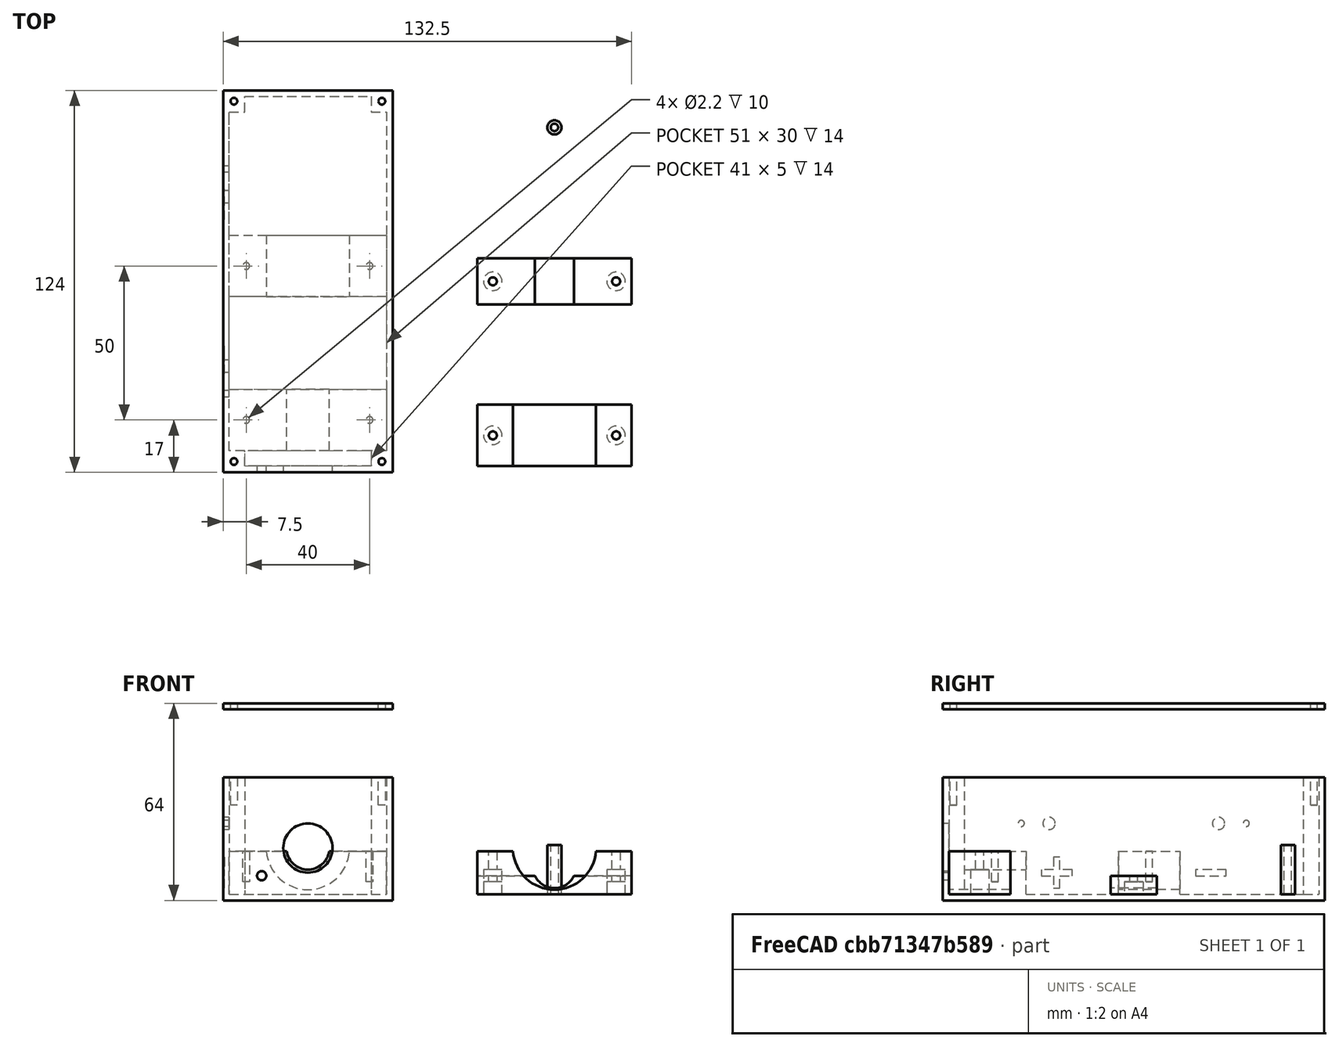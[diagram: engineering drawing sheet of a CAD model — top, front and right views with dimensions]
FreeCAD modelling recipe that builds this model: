
FCSTD DOCUMENT  (FreeCAD 0.20R29410 (Git))
Label: smoker_parts
License: All rights reserved
LicenseURL: http://en.wikipedia.org/wiki/All_rights_reserved
objects: Sketcher::SketchObject×23, PartDesign::Pocket×17, PartDesign::Pad×6, PartDesign::Body×5, Mesh::Feature×5
note: 74 computed .brp shape members not serialized (recipe doc carries the construction recipe); baked Part::Feature solids carry a one-line shape summary decoded from their .brp

FEATURE [Sketcher::SketchObject] Sketch
  FullyConstrained = true
  MapMode = 5
  Support = -> [XY_Plane]
  sketch-geometry (4):
    g0: LineSegment StartX=-25 StartY=7.5 StartZ=0 EndX=25 EndY=7.5 EndZ=0
    g1: LineSegment StartX=25 StartY=7.5 StartZ=0 EndX=25 EndY=-7.5 EndZ=0
    g2: LineSegment StartX=25 StartY=-7.5 StartZ=0 EndX=-25 EndY=-7.5 EndZ=0
    g3: LineSegment StartX=-25 StartY=-7.5 StartZ=0 EndX=-25 EndY=7.5 EndZ=0
  constraints (12):
    c: Coincident(g0,g1)
    c: Coincident(g1,g2)
    c: Coincident(g2,g3)
    c: Coincident(g3,g0)
    c: Horizontal(g0)
    c: Horizontal(g2)
    c: Vertical(g1)
    c: Vertical(g3)
    c: DistanceX(g0,g0) = 50
    c: DistanceY(g1,g1) = 15
    c: DistanceX(g-1,g0) = 25
    c: DistanceY(g1,g-1) = 7.5
FEATURE [PartDesign::Pad] Pad
  Direction = (1,1,1)
  Length = 6
  Length2 = 100
  Profile = -> Sketch
  Type = 0
FEATURE [Sketcher::SketchObject] Sketch001
  FullyConstrained = true
  MapMode = 5
  Placement = pos=(0,-7.5,0) rot=(1,0,0;1.5708rad)
  Support = -> [Pad]
  sketch-geometry (1):
    g0: Circle CenterX=0 CenterY=9 CenterZ=0 NormalX=0 NormalY=0 NormalZ=1 AngleXU=0 Radius=7
  constraints (3):
    c: PointOnObject(g0,g-2)
    c: Radius(g0) = 7
    c: DistanceY(g-1,g0) = 9
FEATURE [PartDesign::Pocket] Pocket
  BaseFeature = -> Pad
  Direction = (1,1,1)
  Length = 5
  Length2 = 100
  Profile = -> Sketch001
  Type = 1
FEATURE [Sketcher::SketchObject] Sketch002
  FullyConstrained = true
  MapMode = 5
  Placement = pos=(0,0,6) rot=(0,0,1;0rad)
  Support = -> [Pad]
  sketch-geometry (2):
    g0: Circle CenterX=-20 CenterY=0 CenterZ=0 NormalX=0 NormalY=0 NormalZ=1 AngleXU=0 Radius=1.3
    g1: Circle CenterX=20 CenterY=0 CenterZ=0 NormalX=0 NormalY=0 NormalZ=1 AngleXU=0 Radius=1.3
  constraints (6):
    c: PointOnObject(g0,g-1)
    c: PointOnObject(g1,g-1)
    c: Equal(g1,g0)
    c: Radius(g0) = 1.3
    c: DistanceX(g0,g1) = 40
    c: DistanceX(g-1,g1) = 20
FEATURE [PartDesign::Pocket] Pocket001
  BaseFeature = -> Pocket
  Direction = (1,1,1)
  Length = 5
  Length2 = 100
  Profile = -> Sketch002
  Type = 1
FEATURE [Sketcher::SketchObject] Sketch003
  FullyConstrained = true
  MapMode = 5
  Support = -> [XY_Plane001]
  sketch-geometry (4):
    g0: LineSegment StartX=-25 StartY=10 StartZ=0 EndX=25 EndY=10 EndZ=0
    g1: LineSegment StartX=25 StartY=10 StartZ=0 EndX=25 EndY=-10 EndZ=0
    g2: LineSegment StartX=25 StartY=-10 StartZ=0 EndX=-25 EndY=-10 EndZ=0
    g3: LineSegment StartX=-25 StartY=-10 StartZ=0 EndX=-25 EndY=10 EndZ=0
  constraints (12):
    c: Coincident(g0,g1)
    c: Coincident(g1,g2)
    c: Coincident(g2,g3)
    c: Coincident(g3,g0)
    c: Horizontal(g0)
    c: Horizontal(g2)
    c: Vertical(g1)
    c: Vertical(g3)
    c: DistanceX(g0,g0) = 50
    c: DistanceY(g1,g1) = 20
    c: DistanceY(g-1,g0) = 10
    c: DistanceX(g-1,g0) = 25
FEATURE [PartDesign::Pad] Pad001
  Direction = (1,1,1)
  Length = 14
  Length2 = 100
  Profile = -> Sketch003
  Type = 0
FEATURE [Sketcher::SketchObject] Sketch004
  FullyConstrained = true
  MapMode = 5
  Placement = pos=(0,-10,0) rot=(1,0,0;1.5708rad)
  Support = -> [Pad001]
  sketch-geometry (1):
    g0: Circle CenterX=0 CenterY=15 CenterZ=0 NormalX=0 NormalY=0 NormalZ=1 AngleXU=0 Radius=13.5
  constraints (3):
    c: PointOnObject(g0,g-2)
    c: Radius(g0) = 13.5
    c: DistanceY(g-1,g0) = 15
FEATURE [PartDesign::Pocket] Pocket002
  BaseFeature = -> Pad001
  Direction = (1,1,1)
  Length = 5
  Length2 = 100
  Profile = -> Sketch004
  Type = 1
FEATURE [Sketcher::SketchObject] Sketch005
  FullyConstrained = true
  MapMode = 5
  Placement = pos=(0,0,14) rot=(0,0,1;0rad)
  Support = -> [Pocket002]
  sketch-geometry (2):
    g0: Circle CenterX=-20 CenterY=0 CenterZ=0 NormalX=0 NormalY=0 NormalZ=1 AngleXU=0 Radius=1.3
    g1: Circle CenterX=20 CenterY=0 CenterZ=0 NormalX=0 NormalY=0 NormalZ=1 AngleXU=0 Radius=1.3
  constraints (6):
    c: PointOnObject(g0,g-1)
    c: PointOnObject(g1,g-1)
    c: Equal(g1,g0)
    c: Radius(g0) = 1.3
    c: DistanceX(g0,g1) = 40
    c: DistanceX(g-1,g1) = 20
FEATURE [PartDesign::Pocket] Pocket003
  BaseFeature = -> Pocket002
  Direction = (1,1,1)
  Length = 5
  Length2 = 100
  Profile = -> Sketch005
  Type = 1
FEATURE [Sketcher::SketchObject] Sketch006
  FullyConstrained = true
  MapMode = 5
  Support = -> [XY_Plane002]
  sketch-geometry (4):
    g0: LineSegment StartX=-27.5 StartY=62 StartZ=0 EndX=27.5 EndY=62 EndZ=0
    g1: LineSegment StartX=27.5 StartY=62 StartZ=0 EndX=27.5 EndY=-62 EndZ=0
    g2: LineSegment StartX=27.5 StartY=-62 StartZ=0 EndX=-27.5 EndY=-62 EndZ=0
    g3: LineSegment StartX=-27.5 StartY=-62 StartZ=0 EndX=-27.5 EndY=62 EndZ=0
  constraints (12):
    c: Coincident(g0,g1)
    c: Coincident(g1,g2)
    c: Coincident(g2,g3)
    c: Coincident(g3,g0)
    c: Horizontal(g0)
    c: Horizontal(g2)
    c: Vertical(g1)
    c: Vertical(g3)
    c: DistanceX(g0,g0) = 55
    c: DistanceX(g-1,g0) = 27.5
    c: DistanceY(g1,g1) = 124
    c: DistanceY(g1,g-1) = 62
FEATURE [PartDesign::Pad] Pad002
  Direction = (1,1,1)
  Length = 40
  Length2 = 100
  Profile = -> Sketch006
  Type = 0
FEATURE [Sketcher::SketchObject] Sketch007
  FullyConstrained = true
  MapMode = 5
  Placement = pos=(0,0,40) rot=(0,0,1;0rad)
  Support = -> [Pad002]
  sketch-geometry (12):
    g0: LineSegment StartX=-25.5 StartY=55 StartZ=0 EndX=-20.5 EndY=55 EndZ=0
    g1: LineSegment StartX=-20.5 StartY=55 StartZ=0 EndX=-20.5 EndY=60 EndZ=0
    g2: LineSegment StartX=-20.5 StartY=60 StartZ=0 EndX=20.5 EndY=60 EndZ=0
    g3: LineSegment StartX=20.5 StartY=60 StartZ=0 EndX=20.5 EndY=55 EndZ=0
    g4: LineSegment StartX=20.5 StartY=55 StartZ=0 EndX=25.5 EndY=55 EndZ=0
    g5: LineSegment StartX=25.5 StartY=55 StartZ=0 EndX=25.5 EndY=-55 EndZ=0
    g6: LineSegment StartX=25.5 StartY=-55 StartZ=0 EndX=20.5 EndY=-55 EndZ=0
    g7: LineSegment StartX=20.5 StartY=-55 StartZ=0 EndX=20.5 EndY=-60 EndZ=0
    g8: LineSegment StartX=20.5 StartY=-60 StartZ=0 EndX=-20.5 EndY=-60 EndZ=0
    g9: LineSegment StartX=-20.5 StartY=-60 StartZ=0 EndX=-20.5 EndY=-55 EndZ=0
    g10: LineSegment StartX=-20.5 StartY=-55 StartZ=0 EndX=-25.5 EndY=-55 EndZ=0
    g11: LineSegment StartX=-25.5 StartY=-55 StartZ=0 EndX=-25.5 EndY=55 EndZ=0
  constraints (36):
    c: Coincident(g0,g1)
    c: Vertical(g1)
    c: Coincident(g1,g2)
    c: Horizontal(g2)
    c: Coincident(g2,g3)
    c: Coincident(g3,g4)
    c: Horizontal(g4)
    c: Coincident(g4,g5)
    c: Vertical(g5)
    c: Coincident(g5,g6)
    c: Coincident(g6,g7)
    c: Coincident(g7,g8)
    c: Horizontal(g8)
    c: Coincident(g8,g9)
    c: Coincident(g9,g10)
    c: Horizontal(g10)
    c: Coincident(g10,g11)
    c: Coincident(g11,g0)
    c: Vertical(g11)
    c: Horizontal(g0)
    c: Vertical(g3)
    c: Horizontal(g6)
    c: Vertical(g7)
    c: Vertical(g9)
    c: Equal(g6,g10)
    c: Equal(g4,g0)
    c: Equal(g1,g3)
    c: DistanceX(g6,g6) = 5
    c: DistanceY(g7,g7) = 5
    c: DistanceX(g2,g2) = 41
    c: DistanceX(g-1,g2) = 20.5
    c: DistanceX(g4,g4) = 5
    c: DistanceY(g3,g3) = 5
    c: DistanceY(g9,g9) = 5
    c: DistanceY(g5,g5) = 110
    c: DistanceY(g-1,g4) = 55
FEATURE [PartDesign::Pocket] Pocket004
  BaseFeature = -> Pad002
  Direction = (1,1,1)
  Length = 38
  Length2 = 100
  Profile = -> Sketch007
  Type = 0
FEATURE [Sketcher::SketchObject] Sketch008
  FullyConstrained = true
  MapMode = 5
  Placement = pos=(0,-62,0) rot=(1,0,0;1.5708rad)
  Support = -> [Pocket004]
  sketch-geometry (1):
    g0: Circle CenterX=0 CenterY=17 CenterZ=0 NormalX=0 NormalY=0 NormalZ=1 AngleXU=0 Radius=8
  constraints (3):
    c: PointOnObject(g0,g-2)
    c: Radius(g0) = 8
    c: DistanceY(g-1,g0) = 17
FEATURE [Sketcher::SketchObject] Sketch014
  FullyConstrained = true
  MapMode = 5
  Support = -> [XY_Plane004]
  sketch-geometry (4):
    g0: LineSegment StartX=-27.5 StartY=62 StartZ=0 EndX=27.5 EndY=62 EndZ=0
    g1: LineSegment StartX=27.5 StartY=62 StartZ=0 EndX=27.5 EndY=-62 EndZ=0
    g2: LineSegment StartX=27.5 StartY=-62 StartZ=0 EndX=-27.5 EndY=-62 EndZ=0
    g3: LineSegment StartX=-27.5 StartY=-62 StartZ=0 EndX=-27.5 EndY=62 EndZ=0
  constraints (12):
    c: Coincident(g0,g1)
    c: Coincident(g1,g2)
    c: Coincident(g2,g3)
    c: Coincident(g3,g0)
    c: Horizontal(g0)
    c: Horizontal(g2)
    c: Vertical(g1)
    c: Vertical(g3)
    c: DistanceX(g0,g0) = 55
    c: DistanceY(g1,g1) = 124
    c: DistanceX(g-1,g0) = 27.5
    c: DistanceY(g-1,g0) = 62
FEATURE [PartDesign::Pad] Pad004
  Direction = (1,1,1)
  Length = 2
  Length2 = 100
  Profile = -> Sketch014
  Type = 0
FEATURE [Sketcher::SketchObject] Sketch015
  FullyConstrained = true
  MapMode = 5
  Placement = pos=(0,0,2) rot=(0,0,1;0rad)
  Support = -> [Pad004]
  sketch-geometry (4):
    g0: Circle CenterX=-24 CenterY=58.5 CenterZ=0 NormalX=0 NormalY=0 NormalZ=1 AngleXU=0 Radius=1.1
    g1: Circle CenterX=24 CenterY=58.5 CenterZ=0 NormalX=0 NormalY=0 NormalZ=1 AngleXU=0 Radius=1.1
    g2: Circle CenterX=-24 CenterY=-58.5 CenterZ=0 NormalX=0 NormalY=0 NormalZ=1 AngleXU=0 Radius=1.1
    g3: Circle CenterX=24 CenterY=-58.5 CenterZ=0 NormalX=0 NormalY=0 NormalZ=1 AngleXU=0 Radius=1.1
  constraints (12):
    c: Radius(g0) = 1.1
    c: Equal(g0,g1)
    c: Equal(g2,g0)
    c: Equal(g0,g3)
    c: DistanceX(g0,g1) = 48
    c: DistanceX(g2,g0) = 0
    c: DistanceX(g0,g-1) = 24
    c: DistanceY(g1,g0) = 0
    c: DistanceY(g-1,g0) = 58.5
    c: DistanceY(g2,g0) = 117
    c: DistanceY(g2,g3) = 0
    c: DistanceX(g2,g3) = 48
FEATURE [PartDesign::Pocket] Pocket010
  BaseFeature = -> Pad004
  Direction = (1,1,1)
  Length = 2
  Length2 = 100
  Profile = -> Sketch015
  Type = 0
FEATURE [PartDesign::Body] Body004  label="Enclosure_lid"
  Group = -> [Sketch014,Pad004,Sketch015,Pocket010]
  Origin = -> Origin004
  Placement = pos=(0,0,60) rot=(0,0,1;0rad)
  Tip = -> Pocket010
FEATURE [Sketcher::SketchObject] Sketch017
  FullyConstrained = true
  MapMode = 5
  Placement = pos=(0,0,0) rot=(1,0,0;3.14159rad)
  Support = -> [Pocket003]
  sketch-geometry (2):
    g0: Circle CenterX=-20 CenterY=0 CenterZ=0 NormalX=0 NormalY=0 NormalZ=1 AngleXU=0 Radius=3
    g1: Circle CenterX=20 CenterY=0 CenterZ=0 NormalX=0 NormalY=0 NormalZ=1 AngleXU=0 Radius=3
  constraints (6):
    c: PointOnObject(g0,g-1)
    c: PointOnObject(g1,g-1)
    c: Radius(g0) = 3
    c: Equal(g0,g1)
    c: DistanceX(g0,g1) = 40
    c: DistanceX(g-1,g1) = 20
FEATURE [PartDesign::Pocket] Pocket012
  BaseFeature = -> Pocket003
  Direction = (1,1,1)
  Length = 8
  Length2 = 100
  Profile = -> Sketch017
  Type = 0
FEATURE [PartDesign::Body] Body001  label="pump"
  Group = -> [Sketch003,Pad001,Sketch004,Pocket002,Sketch005,Pocket003,Sketch017,Pocket012]
  Origin = -> Origin001
  Placement = pos=(80,-50,0) rot=(0,0,1;0rad)
  Tip = -> Pocket012
FEATURE [Sketcher::SketchObject] Sketch018
  FullyConstrained = true
  MapMode = 5
  Placement = pos=(0,0,0) rot=(1,0,0;3.14159rad)
  Support = -> [Pocket001]
  sketch-geometry (2):
    g0: Circle CenterX=-20 CenterY=0 CenterZ=0 NormalX=0 NormalY=0 NormalZ=1 AngleXU=0 Radius=3
    g1: Circle CenterX=20 CenterY=0 CenterZ=0 NormalX=0 NormalY=0 NormalZ=1 AngleXU=0 Radius=3
  constraints (6):
    c: PointOnObject(g0,g-1)
    c: PointOnObject(g1,g-1)
    c: Radius(g0) = 3
    c: Equal(g0,g1)
    c: DistanceX(g0,g1) = 40
    c: DistanceX(g-1,g1) = 20
FEATURE [PartDesign::Pocket] Pocket013
  BaseFeature = -> Pocket001
  Direction = (1,1,1)
  Length = 4
  Length2 = 100
  Profile = -> Sketch018
  Type = 0
FEATURE [PartDesign::Body] Body  label="chamber"
  Group = -> [Sketch,Pad,Sketch001,Pocket,Sketch002,Pocket001,Sketch018,Pocket013]
  Origin = -> Origin
  Placement = pos=(80,0,0) rot=(0,0,1;0rad)
  Tip = -> Pocket013
FEATURE [PartDesign::Pocket] Pocket005
  BaseFeature = -> Pocket004
  Direction = (1,1,1)
  Length = 2
  Length2 = 100
  Profile = -> Sketch008
  Type = 0
FEATURE [Sketcher::SketchObject] Sketch009
  FullyConstrained = true
  MapMode = 5
  Placement = pos=(0,0,40) rot=(0,0,1;0rad)
  Support = -> [Pocket005]
  sketch-geometry (4):
    g0: Circle CenterX=-24 CenterY=58.5 CenterZ=0 NormalX=0 NormalY=0 NormalZ=1 AngleXU=0 Radius=1.1
    g1: Circle CenterX=24 CenterY=58.5 CenterZ=0 NormalX=0 NormalY=0 NormalZ=1 AngleXU=0 Radius=1.1
    g2: Circle CenterX=24 CenterY=-58.5 CenterZ=0 NormalX=0 NormalY=0 NormalZ=1 AngleXU=0 Radius=1.1
    g3: Circle CenterX=-24 CenterY=-58.5 CenterZ=0 NormalX=0 NormalY=0 NormalZ=1 AngleXU=0 Radius=1.1
  constraints (12):
    c: Equal(g1,g0)
    c: Equal(g3,g0)
    c: Equal(g2,g0)
    c: Radius(g0) = 1.1
    c: DistanceY(g0,g1) = 0
    c: DistanceX(g0,g1) = 48
    c: DistanceX(g3,g2) = 48
    c: DistanceY(g3,g2) = 0
    c: DistanceX(g0,g3) = 0
    c: DistanceY(g3,g0) = 117
    c: DistanceX(g3,g-1) = 24
    c: DistanceY(g3,g-1) = 58.5
FEATURE [PartDesign::Pocket] Pocket006
  BaseFeature = -> Pocket005
  Direction = (1,1,1)
  Length = 9
  Length2 = 100
  Profile = -> Sketch009
  Type = 0
FEATURE [Sketcher::SketchObject] Sketch012
  FullyConstrained = true
  MapMode = 5
  Placement = pos=(-27.5,0,0) rot=(0.57735,-0.57735,-0.57735;2.0944rad)
  Support = -> [Pocket006]
  sketch-geometry (4):
    g0: Circle CenterX=-27.5 CenterY=25 CenterZ=0 NormalX=0 NormalY=0 NormalZ=1 AngleXU=0 Radius=2
    g1: Circle CenterX=27.5 CenterY=25 CenterZ=0 NormalX=0 NormalY=0 NormalZ=1 AngleXU=0 Radius=2
    g2: Circle CenterX=-36.5 CenterY=25 CenterZ=0 NormalX=0 NormalY=0 NormalZ=1 AngleXU=0 Radius=1
    g3: Circle CenterX=36.5 CenterY=25 CenterZ=0 NormalX=0 NormalY=0 NormalZ=1 AngleXU=0 Radius=1
  constraints (12):
    c: DistanceX(g0,g1) = 55
    c: DistanceY(g1,g0) = 0
    c: Equal(g1,g0)
    c: Radius(g0) = 2
    c: DistanceX(g2,g3) = 73
    c: DistanceY(g2,g3) = 0
    c: DistanceY(g1,g3) = 0
    c: Equal(g3,g2)
    c: Radius(g3) = 1
    c: DistanceX(g-1,g1) = 27.5
    c: DistanceX(g-1,g3) = 36.5
    c: DistanceY(g-1,g1) = 25
FEATURE [PartDesign::Pocket] Pocket008
  BaseFeature = -> Pocket006
  Direction = (1,1,1)
  Length = 2
  Length2 = 100
  Profile = -> Sketch012
  Type = 0
FEATURE [Sketcher::SketchObject] Sketch013
  FullyConstrained = true
  MapMode = 5
  Placement = pos=(0,-62,0) rot=(1,0,0;1.5708rad)
  Support = -> [Pocket008]
  sketch-geometry (1):
    g0: Circle CenterX=-15 CenterY=8 CenterZ=0 NormalX=0 NormalY=0 NormalZ=1 AngleXU=0 Radius=1.5
  constraints (3):
    c: Radius(g0) = 1.5
    c: DistanceX(g0,g-1) = 15
    c: DistanceY(g-1,g0) = 8
FEATURE [PartDesign::Pocket] Pocket009
  BaseFeature = -> Pocket008
  Direction = (1,1,1)
  Length = 2
  Length2 = 100
  Profile = -> Sketch013
  Type = 0
FEATURE [Sketcher::SketchObject] Sketch016
  FullyConstrained = true
  MapMode = 5
  Placement = pos=(-27.5,0,0) rot=(0.57735,-0.57735,-0.57735;2.0944rad)
  Support = -> [Pocket009]
  sketch-geometry (16):
    g0: LineSegment StartX=-30 StartY=10 StartZ=0 EndX=-20 EndY=10 EndZ=0
    g1: LineSegment StartX=-20 StartY=10 StartZ=0 EndX=-20 EndY=8 EndZ=0
    g2: LineSegment StartX=-20 StartY=8 StartZ=0 EndX=-30 EndY=8 EndZ=0
    g3: LineSegment StartX=-30 StartY=8 StartZ=0 EndX=-30 EndY=10 EndZ=0
    g4: LineSegment StartX=20 StartY=10 StartZ=0 EndX=24 EndY=10 EndZ=0
    g5: LineSegment StartX=30 StartY=10 StartZ=0 EndX=30 EndY=8 EndZ=0
    g6: LineSegment StartX=30 StartY=8 StartZ=0 EndX=26 EndY=8 EndZ=0
    g7: LineSegment StartX=20 StartY=8 StartZ=0 EndX=20 EndY=10 EndZ=0
    g8: LineSegment StartX=24 StartY=14 StartZ=0 EndX=26 EndY=14 EndZ=0
    g9: LineSegment StartX=26 StartY=14 StartZ=0 EndX=26 EndY=10 EndZ=0
    g10: LineSegment StartX=26 StartY=4 StartZ=0 EndX=24 EndY=4 EndZ=0
    g11: LineSegment StartX=24 StartY=4 StartZ=0 EndX=24 EndY=8 EndZ=0
    g12: LineSegment StartX=26 StartY=10 StartZ=0 EndX=30 EndY=10 EndZ=0
    g13: LineSegment StartX=24 StartY=10 StartZ=0 EndX=24 EndY=14 EndZ=0
    g14: LineSegment StartX=26 StartY=8 StartZ=0 EndX=26 EndY=4 EndZ=0
    g15: LineSegment StartX=24 StartY=8 StartZ=0 EndX=20 EndY=8 EndZ=0
  constraints (44):
    c: Coincident(g0,g1)
    c: Coincident(g1,g2)
    c: Coincident(g2,g3)
    c: Coincident(g3,g0)
    c: Horizontal(g0)
    c: Horizontal(g2)
    c: Vertical(g1)
    c: Vertical(g3)
    c: DistanceX(g0,g0) = 10
    c: DistanceY(g1,g1) = 2
    c: Coincident(g12,g5)
    c: Coincident(g5,g6)
    c: Coincident(g15,g7)
    c: Coincident(g7,g4)
    c: Horizontal(g4)
    c: Horizontal(g6)
    c: Vertical(g5)
    c: Vertical(g7)
    c: Coincident(g8,g9)
    c: Coincident(g14,g10)
    c: Coincident(g10,g11)
    c: Coincident(g13,g8)
    c: Horizontal(g8)
    c: Horizontal(g10)
    c: Vertical(g9)
    c: Vertical(g11)
    c: DistanceX(g4,g12) = 10
    c: DistanceX(g10,g10) = 2
    c: DistanceY(g14,g9) = 10
    c: DistanceY(g5,g5) = 2
    c: DistanceX(g4,g8) = 4
    c: DistanceY(g4,g8) = 4
    c: DistanceY(g0,g4) = 0
    c: DistanceX(g1,g15) = 40
    c: DistanceX(g1,g-1) = 20
    c: DistanceY(g-1,g1) = 8
    c: Tangent(g4,g12)
    c: Coincident(g13,g4)
    c: Tangent(g11,g13)
    c: Coincident(g9,g12)
    c: Tangent(g9,g14)
    c: Coincident(g6,g14)
    c: Coincident(g15,g11)
    c: Tangent(g6,g15)
FEATURE [PartDesign::Pocket] Pocket011
  BaseFeature = -> Pocket009
  Direction = (1,1,1)
  Length = 0.4
  Length2 = 100
  Profile = -> Sketch016
  Type = 0
FEATURE [Sketcher::SketchObject] Sketch019
  FullyConstrained = true
  MapMode = 5
  Placement = pos=(0,0,2) rot=(0,0,1;0rad)
  Support = -> [Pocket011]
  sketch-geometry (8):
    g0: LineSegment StartX=-25.5 StartY=15 StartZ=0 EndX=25.5 EndY=15 EndZ=0
    g1: LineSegment StartX=25.5 StartY=15 StartZ=0 EndX=25.5 EndY=-5 EndZ=0
    g2: LineSegment StartX=25.5 StartY=-5 StartZ=0 EndX=-25.5 EndY=-5 EndZ=0
    g3: LineSegment StartX=-25.5 StartY=-5 StartZ=0 EndX=-25.5 EndY=15 EndZ=0
    g4: LineSegment StartX=-25.5 StartY=-35 StartZ=0 EndX=25.5 EndY=-35 EndZ=0
    g5: LineSegment StartX=25.5 StartY=-35 StartZ=0 EndX=25.5 EndY=-55 EndZ=0
    g6: LineSegment StartX=25.5 StartY=-55 StartZ=0 EndX=-25.5 EndY=-55 EndZ=0
    g7: LineSegment StartX=-25.5 StartY=-55 StartZ=0 EndX=-25.5 EndY=-35 EndZ=0
  constraints (24):
    c: Coincident(g0,g1)
    c: Coincident(g1,g2)
    c: Coincident(g2,g3)
    c: Coincident(g3,g0)
    c: Horizontal(g0)
    c: Horizontal(g2)
    c: Vertical(g1)
    c: Vertical(g3)
    c: Coincident(g4,g5)
    c: Coincident(g5,g6)
    c: Coincident(g6,g7)
    c: Coincident(g7,g4)
    c: Horizontal(g4)
    c: Horizontal(g6)
    c: Vertical(g5)
    c: Vertical(g7)
    c: DistanceX(g2,g2) = 51
    c: DistanceX(g4,g4) = 51
    c: DistanceX(g-1,g4) = 25.5
    c: DistanceX(g-1,g1) = 25.5
    c: DistanceY(g1,g1) = 20
    c: DistanceY(g5,g5) = 20
    c: DistanceY(g4,g1) = 30
    c: DistanceY(g-1,g0) = 15
FEATURE [PartDesign::Pad] Pad005
  BaseFeature = -> Pocket011
  Direction = (1,1,1)
  Length = 14
  Length2 = 100
  Profile = -> Sketch019
  Type = 0
FEATURE [Sketcher::SketchObject] Sketch020
  FullyConstrained = true
  MapMode = 5
  Placement = pos=(0,-5,0) rot=(1,0,0;1.5708rad)
  Support = -> [Pad005]
  sketch-geometry (1):
    g0: Circle CenterX=0 CenterY=17 CenterZ=0 NormalX=0 NormalY=0 NormalZ=1 AngleXU=0 Radius=13.5
  constraints (3):
    c: PointOnObject(g0,g-2)
    c: Radius(g0) = 13.5
    c: DistanceY(g-1,g0) = 17
FEATURE [Sketcher::SketchObject] Sketch021
  FullyConstrained = true
  MapMode = 5
  Placement = pos=(0,-35,0) rot=(0,0.707107,0.707107;3.14159rad)
  Support = -> [Pad005]
  sketch-geometry (1):
    g0: Circle CenterX=0 CenterY=17 CenterZ=0 NormalX=0 NormalY=0 NormalZ=1 AngleXU=0 Radius=7
  constraints (3):
    c: PointOnObject(g0,g-2)
    c: Radius(g0) = 7
    c: DistanceY(g-1,g0) = 17
FEATURE [PartDesign::Pocket] Pocket014
  BaseFeature = -> Pad005
  Direction = (1,1,1)
  Length = 20
  Length2 = 100
  Profile = -> Sketch020
  Type = 0
FEATURE [PartDesign::Pocket] Pocket015
  BaseFeature = -> Pocket014
  Direction = (1,1,1)
  Length = 20
  Length2 = 100
  Profile = -> Sketch021
  Type = 0
FEATURE [Sketcher::SketchObject] Sketch022
  FullyConstrained = true
  MapMode = 5
  Placement = pos=(0,0,16) rot=(0,0,1;0rad)
  Support = -> [Pocket015]
  sketch-geometry (4):
    g0: Circle CenterX=-20 CenterY=5 CenterZ=0 NormalX=0 NormalY=0 NormalZ=1 AngleXU=0 Radius=1.1
    g1: Circle CenterX=20 CenterY=5 CenterZ=0 NormalX=0 NormalY=0 NormalZ=1 AngleXU=0 Radius=1.1
    g2: Circle CenterX=-20 CenterY=-45 CenterZ=0 NormalX=0 NormalY=0 NormalZ=1 AngleXU=0 Radius=1.1
    g3: Circle CenterX=20 CenterY=-45 CenterZ=0 NormalX=0 NormalY=0 NormalZ=1 AngleXU=0 Radius=1.1
  constraints (12):
    c: Equal(g3,g2)
    c: Equal(g0,g2)
    c: Equal(g1,g0)
    c: Radius(g1) = 1.1
    c: DistanceY(g1,g0) = 0
    c: DistanceY(g2,g3) = 0
    c: DistanceX(g0,g2) = 0
    c: DistanceX(g2,g-1) = 20
    c: DistanceX(g2,g3) = 40
    c: DistanceX(g0,g1) = 40
    c: DistanceY(g2,g0) = 50
    c: DistanceY(g-1,g0) = 5
FEATURE [PartDesign::Pocket] Pocket016
  BaseFeature = -> Pocket015
  Direction = (1,1,1)
  Length = 10
  Length2 = 100
  Profile = -> Sketch022
  Type = 0
FEATURE [PartDesign::Body] Body002  label="Enclosure"
  Group = -> [Sketch006,Pad002,Sketch007,Pocket004,Sketch008,Pocket005,Sketch009,Pocket006,Sketch012,Pocket008,Sketch013,Pocket009,Sketch016,Pocket011,Sketch019,Pad005,Sketch020,Sketch021,Pocket014,Pocket015,Sketch022,Pocket016]
  Origin = -> Origin002
  Placement = pos=(0,0,-2) rot=(0,0,1;0rad)
  Tip = -> Pocket016
FEATURE [Mesh::Feature] Mesh002  label="Enclosure (Meshed)"
FEATURE [Mesh::Feature] Mesh003  label="Enclosure_lid (Meshed)"
FEATURE [Mesh::Feature] Mesh004  label="pump (Meshed)"
FEATURE [Mesh::Feature] Mesh  label="chamber (Meshed)"
FEATURE [Sketcher::SketchObject] Sketch023
  FullyConstrained = true
  MapMode = 5
  Support = -> [XY_Plane005]
  sketch-geometry (1):
    g0: Circle CenterX=0 CenterY=0 CenterZ=0 NormalX=0 NormalY=0 NormalZ=1 AngleXU=0 Radius=2.3
  constraints (2):
    c: Coincident(g0,g-1)
    c: Radius(g0) = 2.3
FEATURE [PartDesign::Pad] Pad006
  Direction = (0,0,1)
  Length = 16
  Length2 = 10
  Profile = -> Sketch023
  ReferenceAxis = -> Sketch023 [N_Axis]
  Type = 0
FEATURE [Sketcher::SketchObject] Sketch024
  FullyConstrained = true
  MapMode = 5
  Placement = pos=(0,0,16) rot=(0,0,1;0rad)
  Support = -> [Pad006]
  sketch-geometry (1):
    g0: Circle CenterX=0 CenterY=0 CenterZ=0 NormalX=0 NormalY=0 NormalZ=1 AngleXU=0 Radius=1.2
  constraints (2):
    c: Coincident(g0,g-1)
    c: Radius(g0) = 1.2
FEATURE [PartDesign::Pocket] Pocket017
  BaseFeature = -> Pad006
  Direction = (0,0,-1)
  Length = 16
  Length2 = 5
  Profile = -> Sketch024
  ReferenceAxis = -> Sketch024 [N_Axis]
  Type = 0
FEATURE [PartDesign::Body] Body005  label="Tubing_Attachment"
  Group = -> [Sketch023,Pad006,Sketch024,Pocket017]
  Origin = -> Origin005
  Placement = pos=(80,50,0) rot=(0,0,1;0rad)
  Tip = -> Pocket017
FEATURE [Mesh::Feature] Mesh005  label="Tubing_Attachment (Meshed)"
